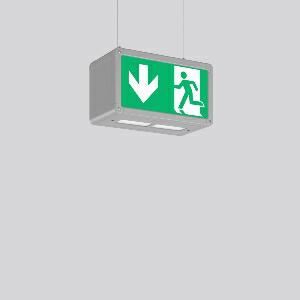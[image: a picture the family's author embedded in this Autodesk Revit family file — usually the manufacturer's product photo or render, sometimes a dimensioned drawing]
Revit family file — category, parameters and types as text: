
# Revit family: rechteck_seilpendel_671343_004_04_9585
name_source: partatom
category: Lighting Fixtures
units: mm (PartAtom-declared; Revit-internal decimal feet)

## family parameters
Cut with Voids When Loaded = No
Host = Face
Light Source = No
Part Type = Normal
Room Calculation Point = No
Round Connector Dimension = Use Diameter
Shared = No

## types (1)
- RECHTECK seilpendel
    Apparent Load = 0 VA
    Default Elevation = 1800 mm
    Description = Series: RECHTECK
Rectangular pendant luminaire in classic design. For escape route identification. Housing: aluminium, with plastic corner connectors. Display panels: plastic, opal, with motifs on one side/on both sides. Pendant luminaires (suspension provided on site) ready for connection to two suspension cables or chains. Driver integrated. Self-contained system with automatic self-test and feedback to the RZB monitoring system MULTIDIGIT. Please indicate legend number when placing your order! 
Colour: anodised aluminium
Length: 250 mm
Width: 125 mm
Height: 140 mm
Weight: 1.62 kg
Operating mode: maintained power mode
Viewing Distance: 21 m
Duration time: 3 h
Lamp: LED
Socket: without socket
Colour temperature: 6500K
Colour rendering index (CRI): 70
System power: 6.9 W
Control gear: Regulated power supply
Protection class: I
Type of protection: IP 44
    Height = 140 mm  [stored 0.459318 ft]
    Lamp = 0 x
    Length = 250 mm
    Luminous efficacy = 0 lm/W
    Manufacturer = RZB
    ModVariant = No
    Model = 671343.004.04
    Mounting Place = Ceiling
    Mounting Type = Pendant
    Number of Poles = 1
    OnlyDefault = Yes
    Power Factor = 1
    Product Name = RECHTECK seilpendel
    Product group = Pendant luminaires
    ProductGroupID = 902
    Protection Class = Protection class I
    Protection Degree = IP 44
    RLX_Detail_Level = 1
    RLX_Emergency_Light_Flux = 0 lm
    RLX_Emergency_Type = 0
    RLX_Emergency_Type_DB = No
    RlxData = <blob elided: 53329 chars, md5=46255263>
    Standby Power = 0 W
    System Light Flux = 0 lm
    System Power = 0 W
    Type Comments = Product without accessories
    Type Image = 671359.004.jpg
    URL = http://relux.com
    VarID = ---
    Voltage = 230 V
    Voltage Range = 220-240 V
    Weight = 0.00 kg
    Width = 125 mm

note: [stored X ft] marks values corroborated as IEEE doubles in the binary element streams (Revit-internal decimal feet)

## geometry (parser evidence)
native form markers: Blend x4, Sweep x10
no freeform markers — native parametric forms only
